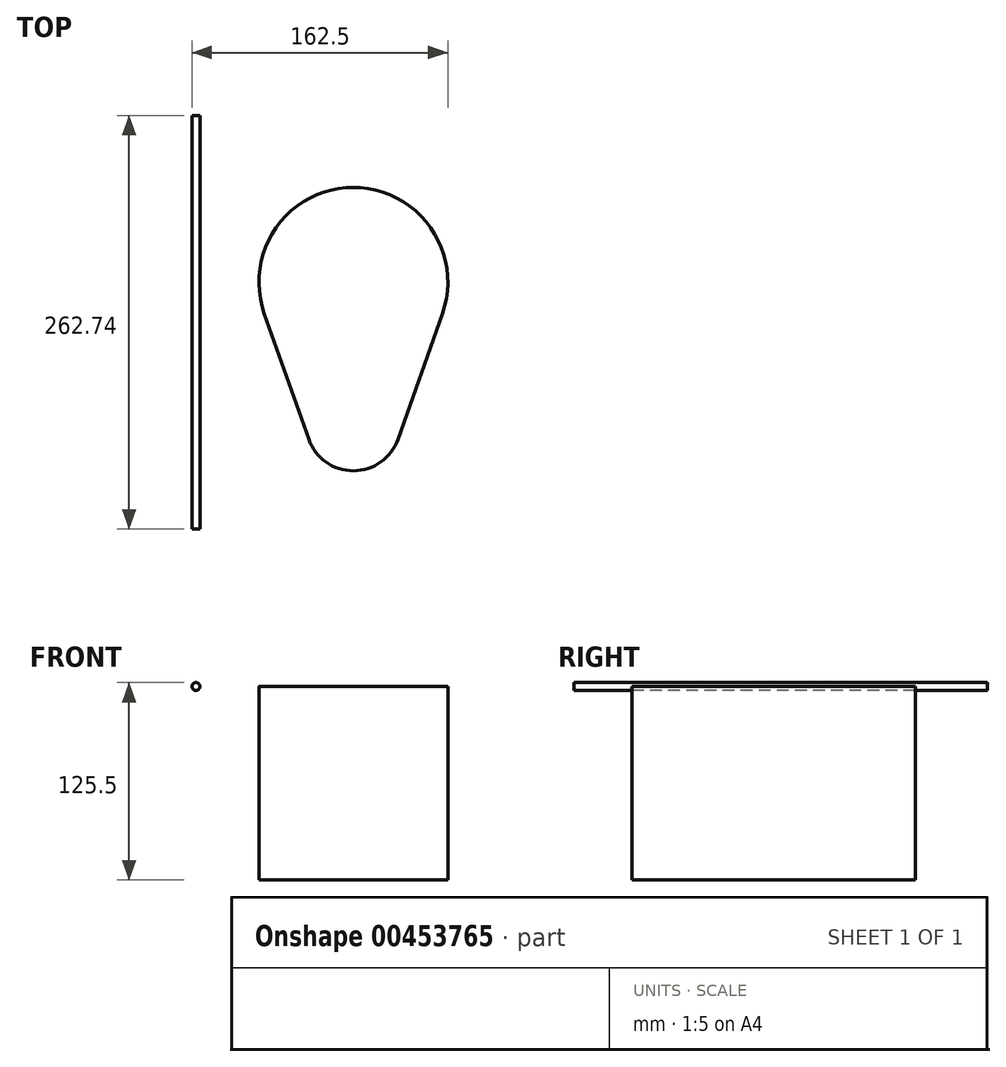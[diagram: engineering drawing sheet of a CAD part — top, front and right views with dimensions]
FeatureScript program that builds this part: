
annotation { "Feature Type Name" : "Feature", "Feature Type Description" : "" }
export const myFeature = defineFeature(function(context is Context, id is Id, definition is map)
    precondition{}
    {
        {
            var Q0;
            Q0=qCreatedBy(makeId("Top.planeOp"),FACE);
            var sketch = newSketch(context, id + "F0", { "sketchPlane" : qUnion([Q0])});
            skArc(sketch, "E0", {"start": v(-28.28, -10) * mm, "mid": v(-17.32, -24.5) * mm, "end": v(0, -30) * mm});
            skArc(sketch, "E1", {"start": v(0, 150) * mm, "mid": v(-48.99, 124.64) * mm, "end": v(-56.57, 70) * mm});
            skLineSegment(sketch, "E2", {"start": v(-56.57, 70) * mm, "end": v(-28.28, -10) * mm});
            skLineSegment(sketch, "E3", {"start": v(0, -61.64) * mm, "end": v(0, 175.09) * mm, "construction": true});
            skArc(sketch, "E4.MirrorCS", {"start": v(0, 150) * mm, "mid": v(48.99, 124.64) * mm, "end": v(56.57, 70) * mm});
            skLineSegment(sketch, "E5.MirrorCS", {"start": v(56.57, 70) * mm, "end": v(28.28, -10) * mm});
            skArc(sketch, "E6.MirrorCS", {"start": v(28.28, -10) * mm, "mid": v(17.32, -24.5) * mm, "end": v(0, -30) * mm});
            skLineSegment(sketch, "E7", {"start": v(-100, -66.99) * mm, "end": v(-100, 195.75) * mm});
            skCircle(sketch, "E8", {"center": v(0, 0) * mm, "radius": 15 * mm});
            skCircle(sketch, "E9", {"center": v(0, 90) * mm, "radius": 45 * mm});
            skCircle(sketch, "E10", {"center": v(0, 0) * mm, "radius": 30 * mm});
            skCircle(sketch, "E11", {"center": v(0, 90) * mm, "radius": 60 * mm});
            skFitSpline(sketch, "E12", {"points": [v(150, -9.7) * mm, v(173.86, 68.78) * mm, v(220.95, 40.07) * mm, v(265.35, 102.09) * mm, v(223.25, 111.66) * mm, v(161.65, 137.83) * mm, v(224.36, 238.69) * mm], "startDerivative": vector(337.36, 638.46) * mm, "endDerivative": vector(501.57, 557.45) * mm});
            skSolve(sketch);
        }
        {
            var Q0;
            Q0=qCreatedBy(makeId("Right.planeOp"),FACE);
            var sketch = newSketch(context, id + "F1", { "sketchPlane" : qUnion([Q0])});
            skLineSegment(sketch, "E13", {"start": v(0, 0) * mm, "end": v(0, -123) * mm});
            skSolve(sketch);
        }
        {
            var Q0;
            Q0=makeQuery(id+"F0.imprint","IMPRINT",FACE,{"disambiguationData":[TD([[makeQuery(id+"F0.imprint","IMPRINT",EDGE,{"derivedFrom":sQuery(id+"F0.wireOp",EDGE,"E8")}),-1.0]])]});
            var Q1;
            Q1=makeQuery(id+"F0.imprint","IMPRINT",FACE,{"disambiguationData":[TD([[makeQuery(id+"F0.imprint","IMPRINT",EDGE,{"derivedFrom":sQuery(id+"F0.wireOp",EDGE,"E9")}),-1.0]])]});
            var Q2;
            {var subQ0=sQuery(id+"F0.wireOp",EDGE,"E5.MirrorCS");Q2=makeQuery(id+"F0.imprint","IMPRINT",FACE,{"disambiguationData":[TD([[makeQuery(id+"F0.imprint","IMPRINT",EDGE,{"derivedFrom":subQ0}),-1.0]])]});}
            var Q3;
            {var subQ0=sQuery(id+"F0.wireOp",EDGE,"E2");Q3=makeQuery(id+"F0.imprint","IMPRINT",FACE,{"disambiguationData":[TD([[makeQuery(id+"F0.imprint","IMPRINT",EDGE,{"derivedFrom":subQ0}),1.0]])]});}
            var Q4;
            Q4=makeQuery(id+"F0.imprint","IMPRINT",FACE,{"disambiguationData":[TD([[makeQuery(id+"F0.imprint","IMPRINT",EDGE,{"derivedFrom":sQuery(id+"F0.wireOp",EDGE,"E9")}),1.0]])]});
            var Q5;
            Q5=makeQuery(id+"F0.imprint","IMPRINT",FACE,{"disambiguationData":[TD([[makeQuery(id+"F0.imprint","IMPRINT",EDGE,{"derivedFrom":sQuery(id+"F0.wireOp",EDGE,"E8")}),1.0]])]});
            var Q6;
            Q6=sQuery(id+"F1.wireOp",EDGE,"E13");
            sweep(context, id + "F2", {"profiles" : qUnion([Q0, Q1, Q2, Q3, Q4, Q5]), "path" : qUnion([Q6])});
        }
        {
            var Q0;
            Q0=qCreatedBy(makeId("Front.planeOp"),FACE);
            cPlane(context, id + "F3", {"entities" : qUnion([Q0]), "cplaneType" : CPlaneType.OFFSET, "offset" : 66.98 * mm, "width" : 150 * mm, "height" : 150 * mm});
        }
        {
            var Q0;
            Q0=qCreatedBy(id+"F3.planeOp",FACE);
            var sketch = newSketch(context, id + "F4", { "sketchPlane" : qUnion([Q0])});
            skPoint(sketch, "E14.0", {"position": v(-100, 0) * mm});
            skCircle(sketch, "E15", {"center": v(-100, 0) * mm, "radius": 2.5 * mm});
            skSolve(sketch);
        }
        {
            var Q0;
            Q0=makeQuery(id+"F4.imprint","IMPRINT",FACE,{"disambiguationData":[TD([[makeQuery(id+"F4.imprint","IMPRINT",EDGE,{"derivedFrom":sQuery(id+"F4.wireOp",EDGE,"E15")}),1.0]])]});
            var Q1;
            Q1=sQuery(id+"F0.wireOp",EDGE,"E7");
            sweep(context, id + "F5", {"profiles" : qUnion([Q0]), "path" : qUnion([Q1])});
        }
    });
